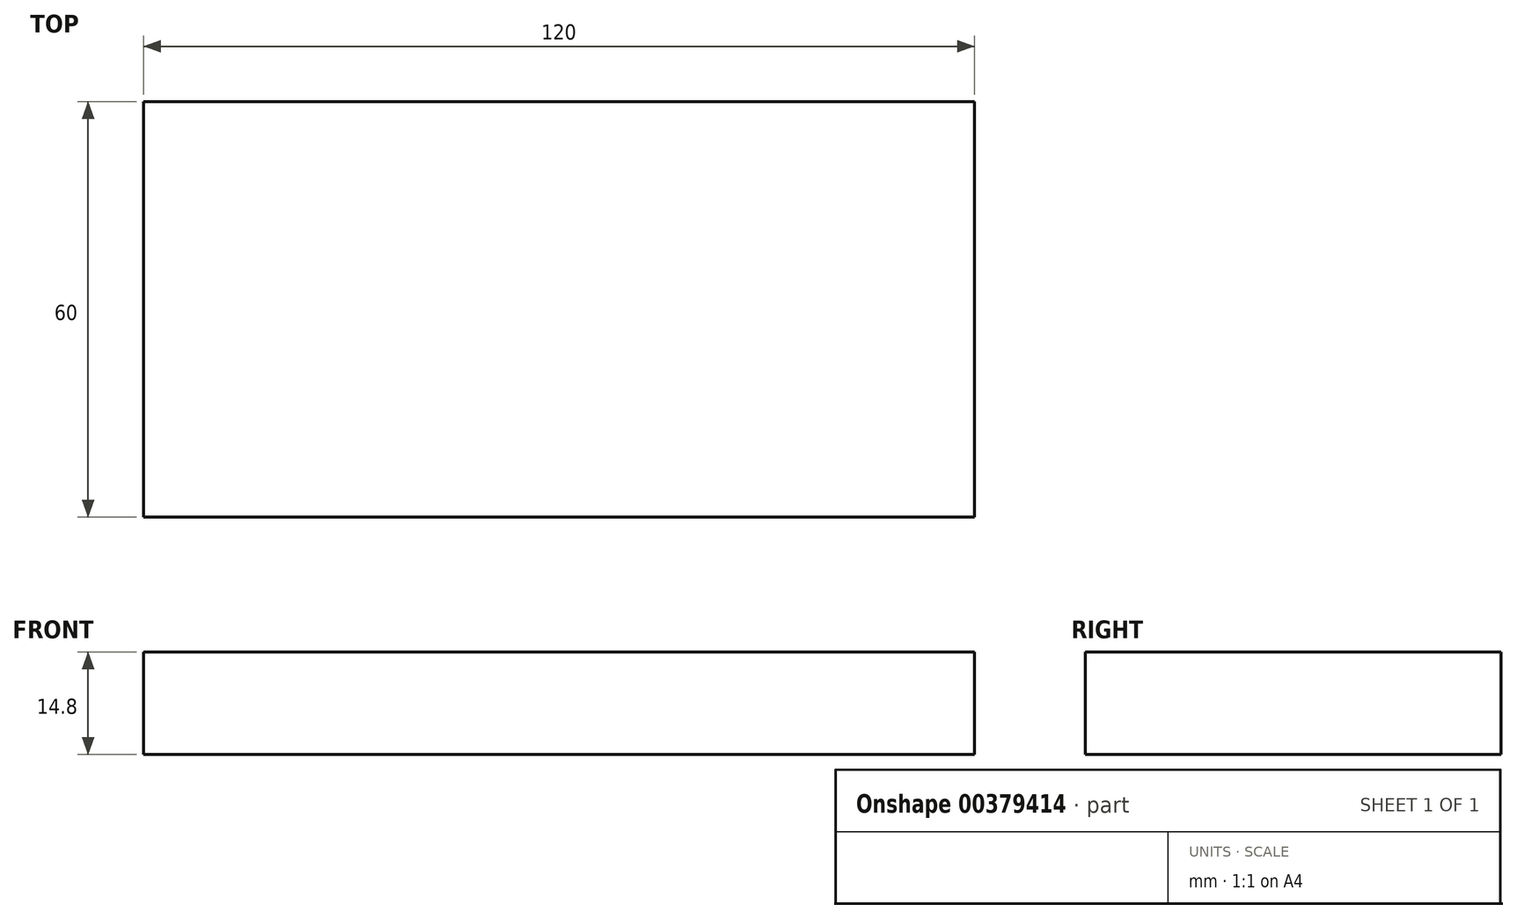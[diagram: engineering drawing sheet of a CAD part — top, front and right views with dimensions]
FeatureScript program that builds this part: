
annotation { "Feature Type Name" : "Feature", "Feature Type Description" : "" }
export const myFeature = defineFeature(function(context is Context, id is Id, definition is map)
    precondition{}
    {
        {
            var Q0;
            Q0=qCreatedBy(makeId("Top.planeOp"),FACE);
            var sketch = newSketch(context, id + "F0", { "sketchPlane" : qUnion([Q0])});
            skLineSegment(sketch, "E0.bottom", {"start": v(58.79, -30.96) * mm, "end": v(-61.21, -30.96) * mm});
            skLineSegment(sketch, "E0.top", {"start": v(58.79, 29.04) * mm, "end": v(-61.21, 29.04) * mm});
            skLineSegment(sketch, "E0.left", {"start": v(58.79, -30.96) * mm, "end": v(58.79, 29.04) * mm});
            skLineSegment(sketch, "E0.right", {"start": v(-61.21, -30.96) * mm, "end": v(-61.21, 29.04) * mm});
            skSolve(sketch);
        }
        {
            var Q0;
            Q0=makeQuery(id+"F0.imprint","IMPRINT",FACE,{"disambiguationData":[TD([[makeQuery(id+"F0.imprint","IMPRINT",EDGE,{"derivedFrom":sQuery(id+"F0.wireOp",EDGE,"E0.bottom")}),-1.0]])]});
            extrude(context, id + "F1", {"entities" : qUnion([Q0]), "endBound" : BoundingType.SYMMETRIC, "depth" : 14.8 * mm});
        }
    });
